# Revit family: BLAUBERG-KOMFORT_Ultra_S_250
name_source: partatom
category: Mechanical Equipment
units: mm (PartAtom-declared; Revit-internal decimal feet)

## family parameters
Always vertical = Yes
Classification = None
Cut with Voids When Loaded = No
OmniClass Number = 23.75.35.14
OmniClass Title = Air Handling Units
Part Type = Normal
Room Calculation Point = No
Round Connector Dimension = Use Diameter
Shared = No
Work Plane-Based = No

## types (2) — shared parameters
B = 287 mm  [stored 0.941601 ft]
B1 = 104 mm
B2 = 104 mm
BackFeetD = 20 mm  [stored 0.0656168 ft]
Casing Material = Painted Steel White
Current = 1 A
D = 125 mm  [stored 0.410105 ft]
Description = Air Handling Unit
DrainConB = 247 mm
Duct Connection Diameter = 125 mm  [stored 0.410105 ft]
ElBoxA = 295 mm  [stored 0.967848 ft]
ElBoxB = 164 mm  [stored 0.538058 ft]
ElConB = 144 mm
ElConH = 182 mm  [stored 0.597113 ft]
Extract Air Filter = G4
Family Version = 1.0
Front Maintenance Zone Height = 500 mm  [stored 1.64042 ft]
H = 419 mm  [stored 1.37467 ft]
HDuctCon = 50 mm  [stored 0.164042 ft]
Heat Exchanger Type = cross-flow
L = 714 mm  [stored 2.34252 ft]
L1 = 80 mm  [stored 0.262467 ft]
L2 = 235 mm  [stored 0.770997 ft]
L3 = 80 mm  [stored 0.262467 ft]
L4 = 235 mm  [stored 0.770997 ft]
Load Classification = HVAC
Maintenance Zone Material = Maintenance Zone
Manufacturer = Blauberg
Maximum Air Flow = 250 m³/h
Maximum Unit Power = 148 W
Metal Material = Metal Zinc
MountingPlateB = 22 mm  [stored 0.0721785 ft]
MountingPlateGapB = 7 mm  [stored 0.0229659 ft]
MountingPlateH1 = 82 mm  [stored 0.269029 ft]
MountingPlateH2 = 343 mm  [stored 1.12533 ft]
Number of Poles = 1
Plastic Material = Polypropylene Black
Power = 148 W
Power Factor = 1
RPM (min-1) = 2700
SEC Class = E
ServiceDoorB = 20 mm  [stored 0.0656168 ft]
Sound Pressure Level at 3 m (dBA) = 28..47
Supply Air Filter = G4 (option F8)
Transported Air Temperature (°C) = -25…+40
URL = https://blaubergventilatoren.de
Unit Current = 1 A
Voltage = 230 V
dBFeets = 70 mm  [stored 0.229659 ft]
dLFeets = 22 mm  [stored 0.0721785 ft]

## per-type parameters (varying)
| type | Drain Connection Diameter | DrainPipe | DrainPipeD | Heat Exchanger Material | Heat recovery efficiency (%) | Type Comments | Weight |
| KOMFORT Ultra S 250-H | 16 mm  [stored 0.0524934 ft] | Yes | 16 mm  [stored 0.0524934 ft] | polystyrene | 55..78 | Air Handling Unit KOMFORT Ultra S 250-H | 26.00 kg |
| KOMFORT Ultra S 250-E | 0 mm  [stored 0 ft] | No | 1 mm  [stored 0.00328084 ft] | enthalpy | 52..73 | Air Handling Unit KOMFORT Ultra S 250-E | 25.00 kg |

note: column(s) folded — value = type name in every type: Model

note: [stored X ft] marks values corroborated as IEEE doubles in the binary element streams (Revit-internal decimal feet)

## geometry (parser evidence)
native form markers: Sweep x7
no freeform markers — native parametric forms only
